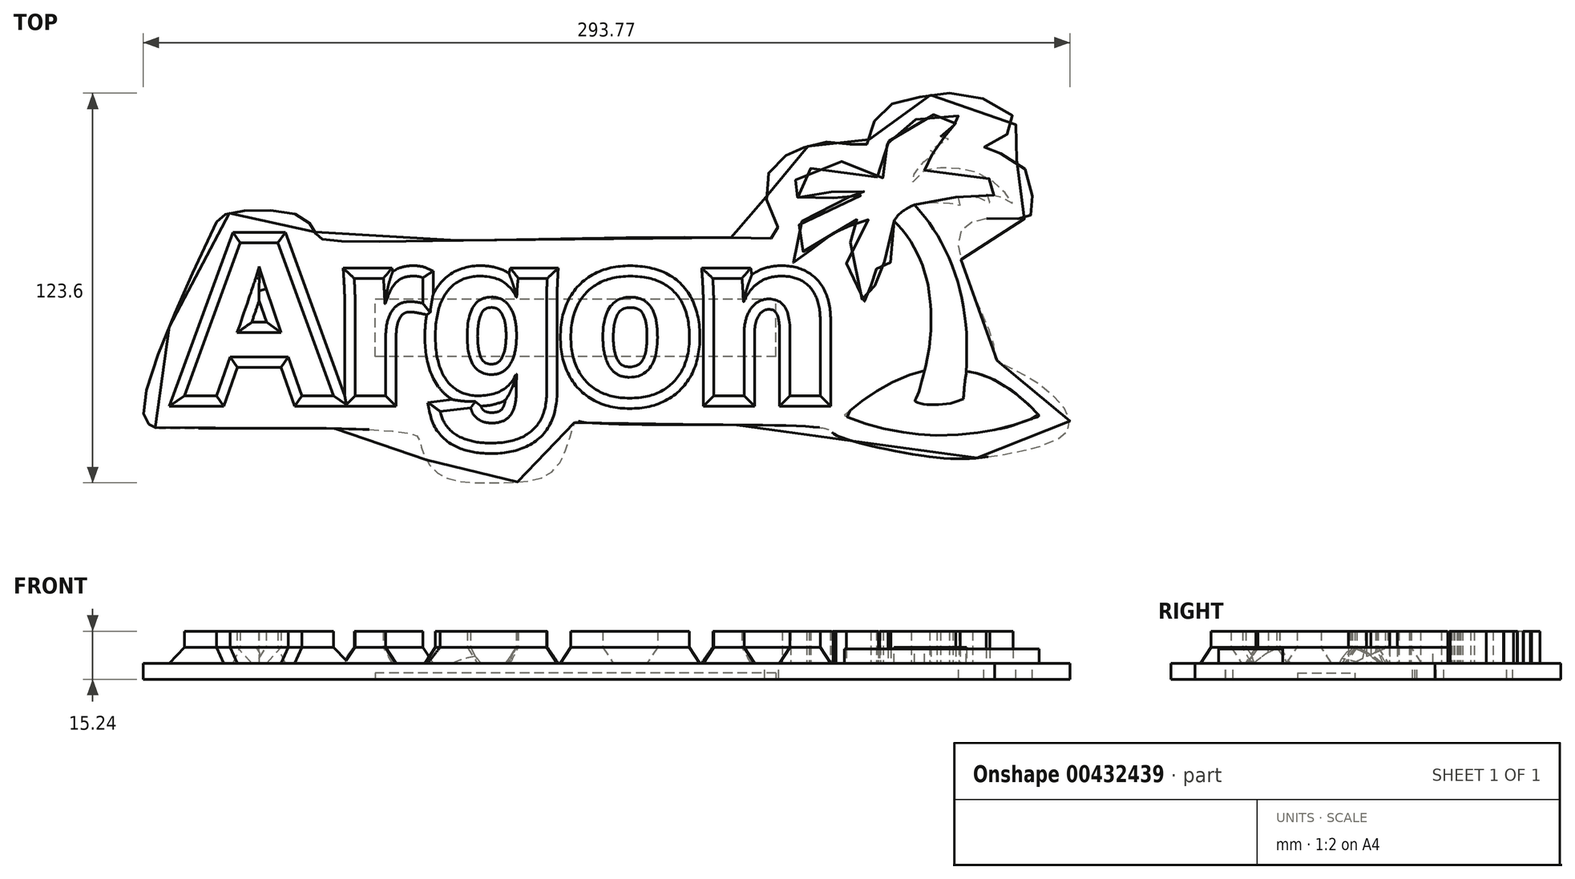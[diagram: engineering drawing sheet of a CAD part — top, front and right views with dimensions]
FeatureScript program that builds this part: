
annotation { "Feature Type Name" : "Feature", "Feature Type Description" : "" }
export const myFeature = defineFeature(function(context is Context, id is Id, definition is map)
    precondition{}
    {
        {
            var Q0;
            Q0=qCreatedBy(makeId("Top.planeOp"),FACE);
            var sketch = newSketch(context, id + "F0", { "sketchPlane" : qUnion([Q0])});
            skText(sketch, "E0", { "text": "Argon", "fontName": "Arimo-Bold.ttf"});
            skFitSpline(sketch, "E1", {"points": [v(223.17, 68.6) * mm, v(219.27, 70.72) * mm, v(214.39, 73.33) * mm, v(209.5, 74.46) * mm, v(204.46, 74.14) * mm, v(200.07, 72.02) * mm, v(195.67, 68.6) * mm, v(193.07, 65.68) * mm, v(191.32, 61.12) * mm, v(193.4, 62.1) * mm, v(196.49, 63.07) * mm, v(199.74, 64.05) * mm, v(199.1, 62.1) * mm, v(202.83, 63.89) * mm, v(207.06, 64.38) * mm, v(206.58, 62.42) * mm, v(208.53, 63.4) * mm, v(213.9, 64.54) * mm, v(218.13, 64.7) * mm, v(221.55, 63.07) * mm, v(217.97, 63.56) * mm, v(215.04, 63.4) * mm, v(211.13, 62.91) * mm, v(207.55, 61.6) * mm, v(202.02, 59.17) * mm, v(196.65, 54.29) * mm, v(195.67, 52.33) * mm, v(194.2, 48.75) * mm, v(194.2, 45.01) * mm, v(195.35, 41.6) * mm, v(197.3, 44.69) * mm, v(198.76, 47.13) * mm, v(200.23, 48.43) * mm, v(200.23, 46.64) * mm, v(201.2, 44.69) * mm, v(202.34, 47.3) * mm, v(204.62, 49.57) * mm, v(205.48, 50.26) * mm, v(207.6, 51.56) * mm, v(207.39, 49.99) * mm, v(208.23, 47.94) * mm, v(208.23, 48.83) * mm, v(210.73, 51.97) * mm, v(214.21, 55.3) * mm, v(218.24, 57.5) * mm, v(221.72, 58.04) * mm, v(220.42, 57.15) * mm, v(216.67, 54.22) * mm, v(213.26, 49.58) * mm, v(211.76, 45) * mm, v(211.76, 41.19) * mm, v(212.71, 37.57) * mm, v(214.35, 34.1) * mm, v(216.12, 31.16) * mm, v(218.78, 29.25) * mm, v(221.78, 28.7) * mm, v(220.7, 30.07) * mm, v(219.8, 32.05) * mm, v(219.4, 34.23) * mm, v(219.6, 35.8) * mm, v(220.83, 34.78) * mm, v(222.2, 34.43) * mm, v(221.65, 35.39) * mm, v(221.1, 38.53) * mm, v(221.24, 41.12) * mm, v(221.85, 43.5) * mm, v(222.06, 44.2) * mm, v(223.35, 42.9) * mm, v(224.99, 41.94) * mm, v(225.74, 41.8) * mm, v(225.26, 43.1) * mm, v(224.79, 45.83) * mm, v(224.92, 50.13) * mm, v(225.8, 53.6) * mm, v(228, 57.22) * mm, v(232.56, 60.36) * mm, v(236.31, 61.25) * mm, v(241.3, 61.45) * mm, v(245.93, 60.7) * mm, v(247.57, 60.15) * mm, v(247.43, 61.04) * mm, v(246.27, 63.09) * mm, v(251.12, 63.22) * mm, v(254.73, 62.47) * mm, v(256.92, 61.25) * mm, v(256.78, 62.6) * mm, v(255.9, 64.04) * mm, v(257.94, 63.77) * mm, v(260.53, 63.16) * mm, v(263.33, 62) * mm, v(264.42, 60.97) * mm, v(262.24, 63.97) * mm, v(259.37, 66.9) * mm, v(255.69, 69.64) * mm, v(250.98, 71.4) * mm, v(246.48, 72.16) * mm, v(241.23, 72.3) * mm, v(237.34, 71.75) * mm, v(234.4, 70.39) * mm, v(232.22, 67.45) * mm, v(232.36, 68.89) * mm, v(234.27, 72.02) * mm, v(236.72, 74.89) * mm, v(238.77, 76.6) * mm, v(240.27, 77.75) * mm, v(239.18, 77.96) * mm, v(238.09, 77.82) * mm, v(239.66, 79.12) * mm, v(243.82, 80.96) * mm, v(244.3, 80.96) * mm, v(243.75, 81.71) * mm, v(242.86, 82.26) * mm, v(241.5, 82.12) * mm, v(242.18, 82.73) * mm, v(243.89, 83.83) * mm, v(245.73, 84.1) * mm, v(247.23, 84.1) * mm, v(247.16, 84.85) * mm, v(246.41, 85.53) * mm, v(245.39, 86.08) * mm, v(246.82, 86.49) * mm, v(249.28, 86.62) * mm, v(251.46, 86.42) * mm, v(250.64, 87.65) * mm, v(243.65, 89.32) * mm, v(243.58, 89.32) * mm, v(240.15, 89.32) * mm, v(236.76, 88.71) * mm, v(233.47, 87.66) * mm, v(231.46, 86.8) * mm, v(229.27, 85.37) * mm, v(226.84, 82.99) * mm, v(224.93, 80.5) * mm, v(223.64, 77.88) * mm, v(222.54, 74.92) * mm, v(222.45, 73.16) * mm, v(222.68, 71.06) * mm, v(223.2, 69.1) * mm, v(223.17, 68.6) * mm]});
            skFitSpline(sketch, "E2", {"points": [v(236.37, 8.04) * mm, v(233.5, 7.29) * mm, v(230.27, 6.14) * mm, v(226.36, 4.42) * mm, v(222.87, 2.5) * mm, v(219.54, 0.62) * mm, v(216.36, -1.78) * mm, v(213.96, -3.55) * mm, v(211.99, -5.42) * mm, v(210.94, -6.26) * mm, v(211.62, -6.62) * mm, v(215.47, -8.08) * mm, v(220.47, -9.54) * mm, v(223.96, -10.47) * mm, v(228.96, -11.41) * mm, v(233.18, -11.98) * mm, v(234.68, -12.14) * mm, v(237.88, -12.46) * mm, v(243.84, -12.46) * mm, v(249.14, -12.09) * mm, v(253.55, -11.55) * mm, v(256.69, -11.06) * mm, v(261.82, -10.17) * mm, v(265.47, -8.94) * mm, v(269.68, -7.44) * mm, v(271.96, -6.66) * mm, v(272.74, -6.4) * mm, v(272.19, -5.7) * mm, v(270.43, -3.8) * mm, v(268.5, -1.97) * mm, v(266.8, -0.61) * mm, v(264.6, 1.35) * mm, v(261.42, 3.36) * mm, v(258.7, 4.94) * mm, v(255.92, 6.2) * mm, v(253.14, 7.15) * mm, v(251.85, 7.45) * mm, v(250.66, 7.7) * mm, v(249.6, 7.76) * mm, v(249.56, 7.42) * mm, v(249.37, 5.76) * mm, v(249, 3.23) * mm, v(248.74, -0.59) * mm, v(248.7, -0.92) * mm], "startDerivative": vector(-120.65, -29.25) * mm, "endDerivative": vector(-7.2, -36.6) * mm});
            skFitSpline(sketch, "E3", {"points": [v(226.68, 55.45) * mm, v(228.02, 54.17) * mm, v(229.83, 52.07) * mm, v(231.88, 49.13) * mm, v(233.4, 46.53) * mm, v(234.7, 43.87) * mm, v(235.61, 41.64) * mm, v(236.32, 39.51) * mm, v(237.24, 36.26) * mm, v(237.82, 33.02) * mm, v(238.14, 30.5) * mm, v(238.4, 27.9) * mm, v(238.43, 25.7) * mm, v(238.44, 22.96) * mm, v(238.33, 19.71) * mm, v(237.73, 14.68) * mm, v(236.75, 9.35) * mm, v(236.37, 8.04) * mm, v(235.27, 3.79) * mm, v(234.76, 1.9) * mm, v(234.23, 0.45) * mm, v(233.48, -1.15) * mm, v(233.29, -1.65) * mm, v(233.57, -1.85) * mm, v(234.68, -2.25) * mm, v(236.37, -2.65) * mm, v(238.16, -2.72) * mm, v(240.68, -2.72) * mm, v(243.17, -2.48) * mm, v(245.45, -2.13) * mm, v(247.48, -1.39) * mm, v(248.7, -0.92) * mm], "startDerivative": vector(45.58, -41.5) * mm, "endDerivative": vector(47.23, 17.53) * mm});
            skFitSpline(sketch, "E4", {"points": [v(249.56, 7.87) * mm, v(249.7, 10.78) * mm, v(249.73, 15.91) * mm, v(249.63, 21.05) * mm, v(248.9, 26.7) * mm, v(247.82, 32.4) * mm, v(246.45, 37.6) * mm, v(244.6, 42.68) * mm, v(242.21, 47.67) * mm, v(240.01, 51.68) * mm, v(237.56, 55.27) * mm, v(235.34, 58.12) * mm, v(233.81, 59.9) * mm, v(233.22, 60.61) * mm], "startDerivative": vector(2.63, 41.89) * mm, "endDerivative": vector(-14.5, 17.73) * mm});
            skLineSegment(sketch, "E5", {"start": v(249.6, 7.76) * mm, "end": v(249.56, 7.87) * mm});
            const initialGuessF0  = {"E0": [0, 0, 1, 0, 0.0508]};
            skSetInitialGuess(sketch, initialGuessF0);
            skSolve(sketch);
        }
        {
            var Q0;
            Q0=makeQuery(id+"F0.imprint","IMPRINT",FACE,{"disambiguationData":[TD([[makeQuery(id+"F0.imprint","IMPRINT",EDGE,{"derivedFrom":sQuery(id+"F0.wireOp",EDGE,"E0.sketch_text.stroke-0")}),-1.0]])]});
            var Q1;
            Q1=makeQuery(id+"F0.imprint","IMPRINT",FACE,{"disambiguationData":[TD([[makeQuery(id+"F0.imprint","IMPRINT",EDGE,{"derivedFrom":sQuery(id+"F0.wireOp",EDGE,"E0.sketch_text.stroke-15")}),-1.0]])]});
            var Q2;
            Q2=makeQuery(id+"F0.imprint","IMPRINT",FACE,{"disambiguationData":[TD([[makeQuery(id+"F0.imprint","IMPRINT",EDGE,{"derivedFrom":sQuery(id+"F0.wireOp",EDGE,"E0.sketch_text.stroke-32")}),-1.0]])]});
            var Q3;
            Q3=makeQuery(id+"F0.imprint","IMPRINT",FACE,{"disambiguationData":[TD([[makeQuery(id+"F0.imprint","IMPRINT",EDGE,{"derivedFrom":sQuery(id+"F0.wireOp",EDGE,"E0.sketch_text.stroke-62")}),-1.0]])]});
            var Q4;
            Q4=makeQuery(id+"F0.imprint","IMPRINT",FACE,{"disambiguationData":[TD([[makeQuery(id+"F0.imprint","IMPRINT",EDGE,{"derivedFrom":sQuery(id+"F0.wireOp",EDGE,"E0.sketch_text.stroke-76")}),-1.0]])]});
            var Q5;
            Q5=makeQuery(id+"F0.imprint","IMPRINT",FACE,{"disambiguationData":[TD([[makeQuery(id+"F0.imprint","IMPRINT",EDGE,{"derivedFrom":sQuery(id+"F0.wireOp",EDGE,"E0.sketch_text.stroke-0")}),-1.0]])]});
            extrude(context, id + "F1", {"entities" : qUnion([Q0, Q1, Q2, Q3, Q4, Q5]), "depth" : 5.08 * mm});
        }
        {
            var Q0;
            Q0=makeQuery(id+"F0.imprint","IMPRINT",FACE,{"disambiguationData":[TD([[makeQuery(id+"F0.imprint","IMPRINT",EDGE,{"derivedFrom":sQuery(id+"F0.wireOp",EDGE,"E0.sketch_text.stroke-0")}),-1.0]])]});
            var Q1;
            Q1=makeQuery(id+"F0.imprint","IMPRINT",FACE,{"disambiguationData":[TD([[makeQuery(id+"F0.imprint","IMPRINT",EDGE,{"derivedFrom":sQuery(id+"F0.wireOp",EDGE,"E0.sketch_text.stroke-33")}),-1.0]])]});
            var Q2;
            Q2=makeQuery(id+"F0.imprint","IMPRINT",FACE,{"disambiguationData":[TD([[makeQuery(id+"F0.imprint","IMPRINT",EDGE,{"derivedFrom":sQuery(id+"F0.wireOp",EDGE,"E0.sketch_text.stroke-28")}),-1.0]])]});
            var Q3;
            Q3=makeQuery(id+"F0.imprint","IMPRINT",FACE,{"disambiguationData":[TD([[makeQuery(id+"F0.imprint","IMPRINT",EDGE,{"derivedFrom":sQuery(id+"F0.wireOp",EDGE,"E0.sketch_text.stroke-37")}),-1.0]])]});
            var Q4;
            Q4=makeQuery(id+"F0.imprint","IMPRINT",FACE,{"disambiguationData":[TD([[makeQuery(id+"F0.imprint","IMPRINT",EDGE,{"derivedFrom":sQuery(id+"F0.wireOp",EDGE,"E0.sketch_text.stroke-41")}),-1.0]])]});
            var Q5;
            Q5=makeQuery(id+"F0.imprint","IMPRINT",FACE,{"disambiguationData":[TD([[makeQuery(id+"F0.imprint","IMPRINT",EDGE,{"derivedFrom":sQuery(id+"F0.wireOp",EDGE,"E0.sketch_text.stroke-66")}),-1.0]])]});
            var Q6;
            Q6=makeQuery(id+"F0.imprint","IMPRINT",FACE,{"disambiguationData":[TD([[makeQuery(id+"F0.imprint","IMPRINT",EDGE,{"derivedFrom":sQuery(id+"F0.wireOp",EDGE,"E0.sketch_text.stroke-83")}),-1.0]])]});
            var Q7;
            Q7=makeQuery(id+"F0.imprint","IMPRINT",FACE,{"disambiguationData":[TD([[makeQuery(id+"F0.imprint","IMPRINT",EDGE,{"derivedFrom":sQuery(id+"F0.wireOp",EDGE,"E0.sketch_text.stroke-12")}),-1.0]])]});
            var Q8;
            Q8=makeQuery(id+"F0.imprint","IMPRINT",FACE,{"disambiguationData":[TD([[makeQuery(id+"F0.imprint","IMPRINT",EDGE,{"derivedFrom":sQuery(id+"F0.wireOp",EDGE,"E0.sketch_text.stroke-87")}),-1.0]])]});
            extrude(context, id + "F2", {"entities" : qUnion([Q0, Q1, Q2, Q3, Q4, Q5, Q6, Q7, Q8]), "operationType" : NewBodyOperationType.ADD, "oppositeDirection" : true, "depth" : 5.08 * mm, "hasDraft" : true, "draftAngle" : 33 * degree});
        }
        {
            var Q0;
            {var subQ7=sQuery(id+"F0.wireOp",EDGE,"E4");Q0=makeQuery(id+"F0.imprint","IMPRINT",FACE,{"disambiguationData":[TD([[makeQuery(id+"F0.imprint","IMPRINT",EDGE,{"derivedFrom":subQ7}),1.0]])]});}
            extrude(context, id + "F3", {"entities" : qUnion([Q0]), "operationType" : NewBodyOperationType.ADD, "oppositeDirection" : true, "depth" : 5.08 * mm});
        }
        {
            var Q0;
            {var subQ0=sQuery(id+"F0.wireOp",EDGE,"E1");var subQ1=makeQuery(id+"F0.imprint","INTERSECT",VERTEX,{"derivedFrom":[subQ0,sQuery(id+"F0.wireOp",EDGE,"E3")]});Q0=makeQuery(id+"F0.imprint","IMPRINT",FACE,{"disambiguationData":[TD([[makeQuery(id+"F0.imprint","IMPRINT",EDGE,{"disambiguationData":[TD([[subQ1,-1.0]])],"derivedFrom":subQ0}),1.0]])]});}
            extrude(context, id + "F4", {"entities" : qUnion([Q0]), "operationType" : NewBodyOperationType.ADD, "depth" : 5.08 * mm});
        }
        {
            var Q0;
            {var subQ0=sQuery(id+"F0.wireOp",EDGE,"E3");var subQ1=sQuery(id+"F0.wireOp",EDGE,"E2");var subQ2=makeQuery(id+"F0.imprint","INTERSECT",VERTEX,{"disambiguationData":[OD(0.0)],"derivedFrom":[subQ1,subQ0]});Q0=makeQuery(id+"F0.imprint","IMPRINT",FACE,{"disambiguationData":[TD([[makeQuery(id+"F0.imprint","IMPRINT",EDGE,{"disambiguationData":[TD([[subQ2,-1.0]])],"derivedFrom":subQ1}),1.0]])]});}
            var Q1;
            {var subQ0=sQuery(id+"F0.wireOp",EDGE,"E1");var subQ1=makeQuery(id+"F0.imprint","INTERSECT",VERTEX,{"derivedFrom":[subQ0,sQuery(id+"F0.wireOp",EDGE,"E3")]});Q1=makeQuery(id+"F0.imprint","IMPRINT",FACE,{"disambiguationData":[TD([[makeQuery(id+"F0.imprint","IMPRINT",EDGE,{"disambiguationData":[TD([[subQ1,-1.0]])],"derivedFrom":subQ0}),1.0]])]});}
            var Q2;
            {var subQ7=sQuery(id+"F0.wireOp",EDGE,"E4");Q2=makeQuery(id+"F0.imprint","IMPRINT",FACE,{"disambiguationData":[TD([[makeQuery(id+"F0.imprint","IMPRINT",EDGE,{"derivedFrom":subQ7}),1.0]])]});}
            extrude(context, id + "F5", {"entities" : qUnion([Q0, Q1, Q2]), "operationType" : NewBodyOperationType.ADD, "oppositeDirection" : true, "depth" : 5.08 * mm});
        }
        {
            var Q0;
            {var subQ0=sQuery(id+"F0.wireOp",EDGE,"E3");var subQ1=sQuery(id+"F0.wireOp",EDGE,"E2");var subQ2=makeQuery(id+"F0.imprint","INTERSECT",VERTEX,{"disambiguationData":[OD(0.0)],"derivedFrom":[subQ1,subQ0]});Q0=makeQuery(id+"F0.imprint","IMPRINT",FACE,{"disambiguationData":[TD([[makeQuery(id+"F0.imprint","IMPRINT",EDGE,{"disambiguationData":[TD([[subQ2,-1.0]])],"derivedFrom":subQ1}),1.0]])]});}
            extrude(context, id + "F6", {"entities" : qUnion([Q0]), "operationType" : NewBodyOperationType.REMOVE, "oppositeDirection" : true, "depth" : 0.5 * mm});
        }
        {
            var Q0;
            Q0=makeQuery(id+"F2.boolean.opBoolean","MERGE",FACE,{"derivedFrom":[makeQuery(id+"F2.opExtrude","CAP_FACE",FACE,{"disambiguationData":[OSD([sQuery(id+"F0.wireOp",EDGE,"E0.sketch_text.stroke-0"),sQuery(id+"F0.wireOp",EDGE,"E0.sketch_text.stroke-1"),sQuery(id+"F0.wireOp",EDGE,"E0.sketch_text.stroke-2"),sQuery(id+"F0.wireOp",EDGE,"E0.sketch_text.stroke-3"),sQuery(id+"F0.wireOp",EDGE,"E0.sketch_text.stroke-4"),sQuery(id+"F0.wireOp",EDGE,"E0.sketch_text.stroke-5"),sQuery(id+"F0.wireOp",EDGE,"E0.sketch_text.stroke-6"),sQuery(id+"F0.wireOp",EDGE,"E0.sketch_text.stroke-7"),sQuery(id+"F0.wireOp",EDGE,"E0.sketch_text.stroke-8"),sQuery(id+"F0.wireOp",EDGE,"E0.sketch_text.stroke-9"),sQuery(id+"F0.wireOp",EDGE,"E0.sketch_text.stroke-10"),sQuery(id+"F0.wireOp",EDGE,"E0.sketch_text.stroke-11"),sQuery(id+"F0.wireOp",EDGE,"E0.sketch_text.stroke-12"),sQuery(id+"F0.wireOp",EDGE,"E0.sketch_text.stroke-13"),sQuery(id+"F0.wireOp",EDGE,"E0.sketch_text.stroke-14")])],"isStart":false}),makeQuery(id+"F2.opExtrude","CAP_FACE",FACE,{"disambiguationData":[OSD([sQuery(id+"F0.wireOp",EDGE,"E0.sketch_text.stroke-15"),sQuery(id+"F0.wireOp",EDGE,"E0.sketch_text.stroke-16"),sQuery(id+"F0.wireOp",EDGE,"E0.sketch_text.stroke-17"),sQuery(id+"F0.wireOp",EDGE,"E0.sketch_text.stroke-18"),sQuery(id+"F0.wireOp",EDGE,"E0.sketch_text.stroke-19"),sQuery(id+"F0.wireOp",EDGE,"E0.sketch_text.stroke-20"),sQuery(id+"F0.wireOp",EDGE,"E0.sketch_text.stroke-21"),sQuery(id+"F0.wireOp",EDGE,"E0.sketch_text.stroke-22"),sQuery(id+"F0.wireOp",EDGE,"E0.sketch_text.stroke-23"),sQuery(id+"F0.wireOp",EDGE,"E0.sketch_text.stroke-24"),sQuery(id+"F0.wireOp",EDGE,"E0.sketch_text.stroke-25"),sQuery(id+"F0.wireOp",EDGE,"E0.sketch_text.stroke-26"),sQuery(id+"F0.wireOp",EDGE,"E0.sketch_text.stroke-27"),sQuery(id+"F0.wireOp",EDGE,"E0.sketch_text.stroke-28"),sQuery(id+"F0.wireOp",EDGE,"E0.sketch_text.stroke-29"),sQuery(id+"F0.wireOp",EDGE,"E0.sketch_text.stroke-30"),sQuery(id+"F0.wireOp",EDGE,"E0.sketch_text.stroke-31")])],"isStart":false}),makeQuery(id+"F2.opExtrude","CAP_FACE",FACE,{"disambiguationData":[OSD([sQuery(id+"F0.wireOp",EDGE,"E0.sketch_text.stroke-32"),sQuery(id+"F0.wireOp",EDGE,"E0.sketch_text.stroke-33"),sQuery(id+"F0.wireOp",EDGE,"E0.sketch_text.stroke-34"),sQuery(id+"F0.wireOp",EDGE,"E0.sketch_text.stroke-35"),sQuery(id+"F0.wireOp",EDGE,"E0.sketch_text.stroke-36"),sQuery(id+"F0.wireOp",EDGE,"E0.sketch_text.stroke-37"),sQuery(id+"F0.wireOp",EDGE,"E0.sketch_text.stroke-38"),sQuery(id+"F0.wireOp",EDGE,"E0.sketch_text.stroke-39"),sQuery(id+"F0.wireOp",EDGE,"E0.sketch_text.stroke-40"),sQuery(id+"F0.wireOp",EDGE,"E0.sketch_text.stroke-41"),sQuery(id+"F0.wireOp",EDGE,"E0.sketch_text.stroke-42"),sQuery(id+"F0.wireOp",EDGE,"E0.sketch_text.stroke-43"),sQuery(id+"F0.wireOp",EDGE,"E0.sketch_text.stroke-44"),sQuery(id+"F0.wireOp",EDGE,"E0.sketch_text.stroke-45"),sQuery(id+"F0.wireOp",EDGE,"E0.sketch_text.stroke-46"),sQuery(id+"F0.wireOp",EDGE,"E0.sketch_text.stroke-47"),sQuery(id+"F0.wireOp",EDGE,"E0.sketch_text.stroke-48"),sQuery(id+"F0.wireOp",EDGE,"E0.sketch_text.stroke-49"),sQuery(id+"F0.wireOp",EDGE,"E0.sketch_text.stroke-50"),sQuery(id+"F0.wireOp",EDGE,"E0.sketch_text.stroke-51"),sQuery(id+"F0.wireOp",EDGE,"E0.sketch_text.stroke-52"),sQuery(id+"F0.wireOp",EDGE,"E0.sketch_text.stroke-53"),sQuery(id+"F0.wireOp",EDGE,"E0.sketch_text.stroke-54"),sQuery(id+"F0.wireOp",EDGE,"E0.sketch_text.stroke-55"),sQuery(id+"F0.wireOp",EDGE,"E0.sketch_text.stroke-56"),sQuery(id+"F0.wireOp",EDGE,"E0.sketch_text.stroke-57"),sQuery(id+"F0.wireOp",EDGE,"E0.sketch_text.stroke-58"),sQuery(id+"F0.wireOp",EDGE,"E0.sketch_text.stroke-59"),sQuery(id+"F0.wireOp",EDGE,"E0.sketch_text.stroke-60"),sQuery(id+"F0.wireOp",EDGE,"E0.sketch_text.stroke-61")])],"isStart":false})]});
            var sketch = newSketch(context, id + "F7", { "sketchPlane" : qUnion([Q0])});
            skFitSpline(sketch, "E6", {"points": [v(175.07, -50.15) * mm, v(48.92, -49.18) * mm, v(43.63, -51.11) * mm, v(38.81, -56.89) * mm, v(15.7, -57.85) * mm, v(10.4, -51.84) * mm, v(-11.26, 3.78) * mm, v(-8.82, 9.43) * mm, v(-3.07, 10.3) * mm, v(73.94, 12.01) * mm, v(76.51, 14.88) * mm, v(82.16, 24.55) * mm, v(102.56, 27.47) * mm, v(119.74, 22.6) * mm, v(125.47, 8.3) * mm, v(128.04, 8.3) * mm, v(204.77, 10.3) * mm, v(207.63, 12.01) * mm, v(237.12, 19.17) * mm, v(261.16, 18.6) * mm, v(282.35, 9.72) * mm, v(270.04, -5.45) * mm, v(258.87, -11.75) * mm, v(258.3, -16.61) * mm, v(247.7, -51.84) * mm, v(264.73, -56.28) * mm, v(269.66, -56.8) * mm, v(270.57, -62.11) * mm, v(265.18, -75.06) * mm, v(255.18, -78.7) * mm, v(265.18, -85.52) * mm, v(252.46, -95.06) * mm, v(233.82, -94.6) * mm, v(221.55, -89.15) * mm, v(217.46, -79.15) * mm, v(210.2, -80.52) * mm, v(199.29, -79.15) * mm, v(192.02, -75.97) * mm, v(185.65, -65.97) * mm, v(190.2, -51.84) * mm, v(175.07, -50.15) * mm]});
            skSolve(sketch);
        }
        {
            var Q0;
            Q0 = qSketchRegion(id + "F7", true);
            extrude(context, id + "F8", {"entities" : qUnion([Q0]), "operationType" : NewBodyOperationType.ADD, "depth" : 5.08 * mm});
        }
        {
            var Q0;
            Q0=makeQuery(id+"F8.opExtrude","CAP_FACE",FACE,{"disambiguationData":[OSD([sQuery(id+"F7.wireOp",EDGE,"E6")])],"isStart":false});
            var sketch = newSketch(context, id + "F9", { "sketchPlane" : qUnion([Q0])});
            skLineSegment(sketch, "E7.bottom", {"start": v(189.3, -12.5) * mm, "end": v(62.3, -12.5) * mm});
            skLineSegment(sketch, "E7.top", {"start": v(189.3, -30.67) * mm, "end": v(62.3, -30.67) * mm});
            skLineSegment(sketch, "E7.left", {"start": v(189.3, -12.5) * mm, "end": v(189.3, -30.67) * mm});
            skLineSegment(sketch, "E7.right", {"start": v(62.3, -12.5) * mm, "end": v(62.3, -30.67) * mm});
            skSolve(sketch);
        }
        {
            var Q0;
            Q0=makeQuery(id+"F9.imprint","IMPRINT",FACE,{"disambiguationData":[TD([[makeQuery(id+"F9.imprint","IMPRINT",EDGE,{"derivedFrom":sQuery(id+"F9.wireOp",EDGE,"E7.bottom")}),1.0]])]});
            extrude(context, id + "F10", {"entities" : qUnion([Q0]), "operationType" : NewBodyOperationType.REMOVE, "oppositeDirection" : true, "depth" : 2 * mm});
        }
    });
